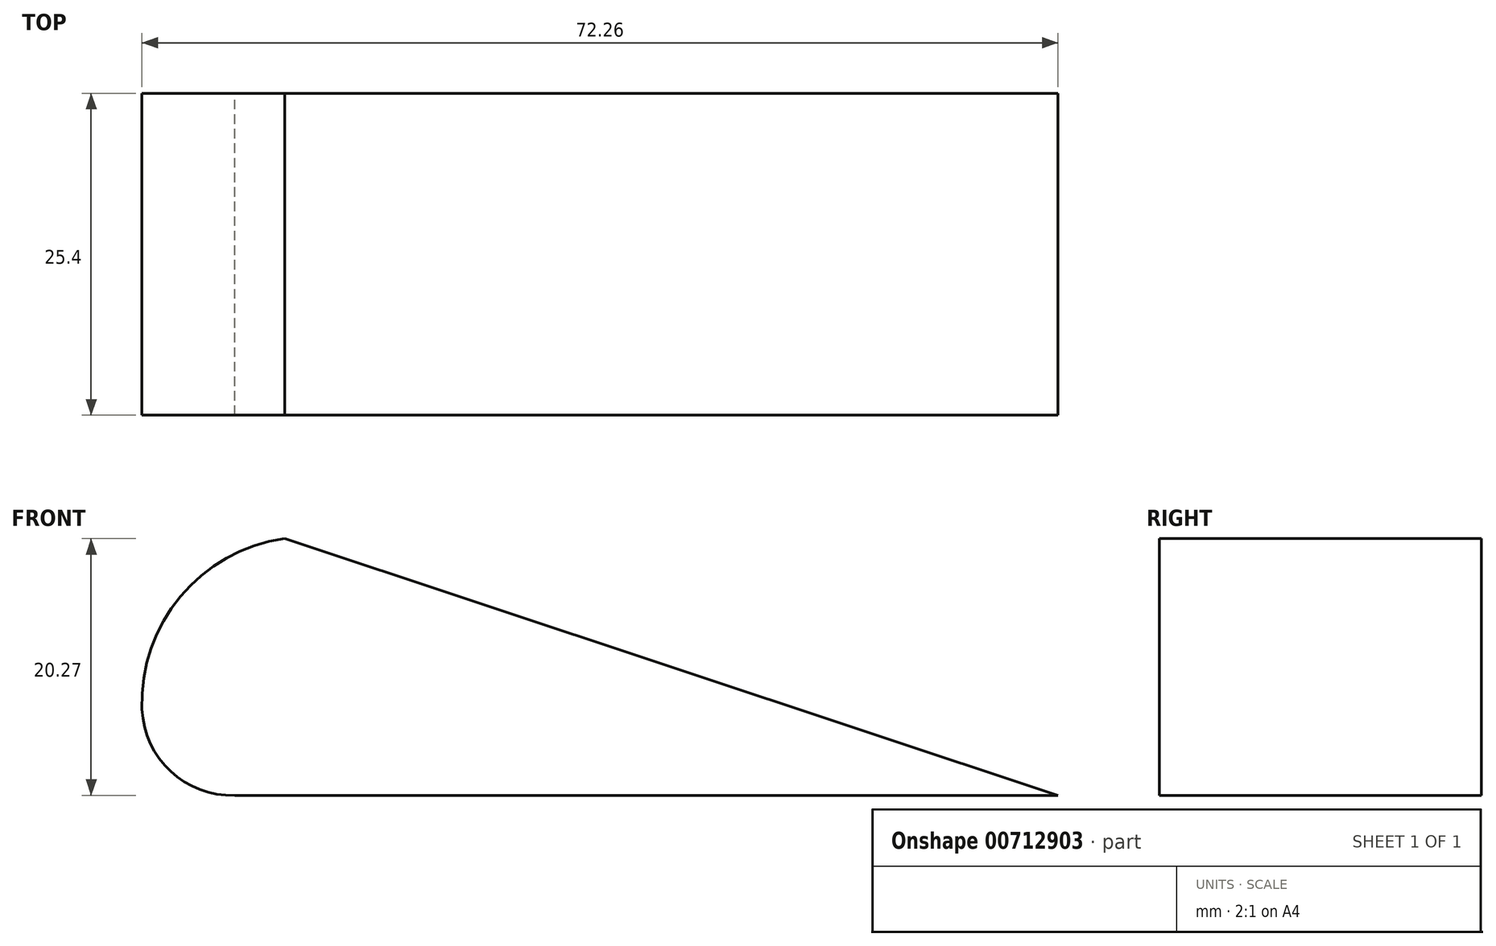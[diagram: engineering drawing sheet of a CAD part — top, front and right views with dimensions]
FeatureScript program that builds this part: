
annotation { "Feature Type Name" : "Feature", "Feature Type Description" : "" }
export const myFeature = defineFeature(function(context is Context, id is Id, definition is map)
    precondition{}
    {
        {
            var Q0;
            Q0=qCreatedBy(makeId("Front.planeOp"),FACE);
            var sketch = newSketch(context, id + "F0", { "sketchPlane" : qUnion([Q0])});
            skLineSegment(sketch, "E0", {"start": v(-28, -14.1) * mm, "end": v(36.93, -14.1) * mm});
            skArc(sketch, "E1", {"start": v(-28, -14.1) * mm, "mid": v(-33.07, -12.22) * mm, "end": v(-35.32, -7.31) * mm});
            skArc(sketch, "E2", {"start": v(-35.32, -7.31) * mm, "mid": v(-32.3, 1.59) * mm, "end": v(-24.08, 6.16) * mm});
            skLineSegment(sketch, "E3", {"start": v(-24.08, 6.16) * mm, "end": v(36.93, -14.1) * mm});
            skSolve(sketch);
        }
        {
            var Q0;
            Q0=makeQuery(id+"F0.imprint","IMPRINT",FACE,{"disambiguationData":[TD([[makeQuery(id+"F0.imprint","IMPRINT",EDGE,{"derivedFrom":sQuery(id+"F0.wireOp",EDGE,"E0")}),1.0]])]});
            var sketch = newSketch(context, id + "F1", { "sketchPlane" : qUnion([Q0])});
            skSolve(sketch);
        }
        {
            var Q0;
            Q0=makeQuery(id+"F1.imprint","IMPRINT",FACE,{"disambiguationData":[TD([[makeQuery(id+"F1.imprint","IMPRINT",EDGE,{"derivedFrom":makeQuery(id+"F0.imprint","IMPRINT",EDGE,{"derivedFrom":sQuery(id+"F0.wireOp",EDGE,"E0")})}),1.0]])]});
            extrude(context, id + "F2", {"entities" : qUnion([Q0]), "depth" : 25.4 * mm, "offsetDistance" : 25.4 * mm});
        }
    });
